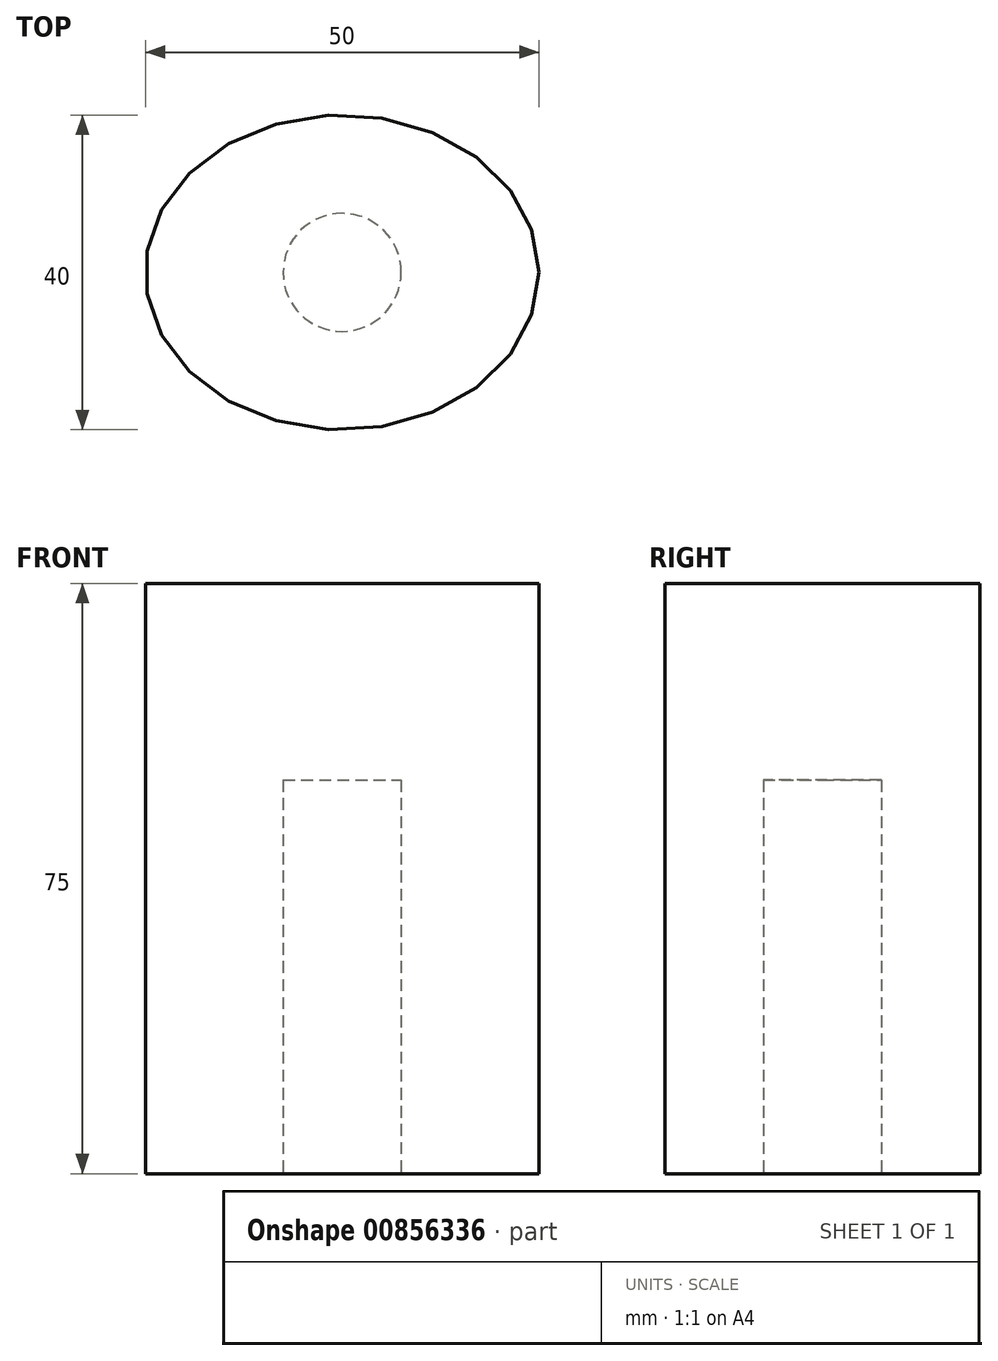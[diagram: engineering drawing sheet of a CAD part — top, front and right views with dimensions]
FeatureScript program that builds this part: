
annotation { "Feature Type Name" : "Feature", "Feature Type Description" : "" }
export const myFeature = defineFeature(function(context is Context, id is Id, definition is map)
    precondition{}
    {
        {
            var Q0;
            Q0=qCreatedBy(makeId("Top.planeOp"),FACE);
            var sketch = newSketch(context, id + "F0", { "sketchPlane" : qUnion([Q0])});
            skEllipse(sketch, "E0", {"center": v(0, 0) * mm, "majorRadius": 25 * mm, "minorRadius": 20 * mm, "majorAxis": v(1, 0)});
            skSolve(sketch);
        }
        {
            var Q0;
            Q0=makeQuery(id+"F0.imprint","IMPRINT",FACE,{"disambiguationData":[TD([[makeQuery(id+"F0.imprint","IMPRINT",EDGE,{"derivedFrom":sQuery(id+"F0.wireOp",EDGE,"E0")}),1.0]])]});
            extrude(context, id + "F1", {"entities" : qUnion([Q0]), "depth" : 75 * mm, "offsetDistance" : 25 * mm});
        }
        {
            var Q0;
            Q0=makeQuery(id+"F1.opExtrude","CAP_FACE",FACE,{"disambiguationData":[OSD([sQuery(id+"F0.wireOp",EDGE,"E0")])],"isStart":true});
            var sketch = newSketch(context, id + "F2", { "sketchPlane" : qUnion([Q0])});
            skCircle(sketch, "E1", {"center": v(0, 0) * mm, "radius": 7.5 * mm});
            skSolve(sketch);
        }
        {
            var Q0;
            Q0=makeQuery(id+"F2.imprint","IMPRINT",FACE,{"disambiguationData":[TD([[makeQuery(id+"F2.imprint","IMPRINT",EDGE,{"derivedFrom":sQuery(id+"F2.wireOp",EDGE,"E1")}),1.0]])]});
            extrude(context, id + "F3", {"entities" : qUnion([Q0]), "operationType" : NewBodyOperationType.REMOVE, "oppositeDirection" : true, "depth" : 50 * mm, "offsetDistance" : 25 * mm});
        }
    });
